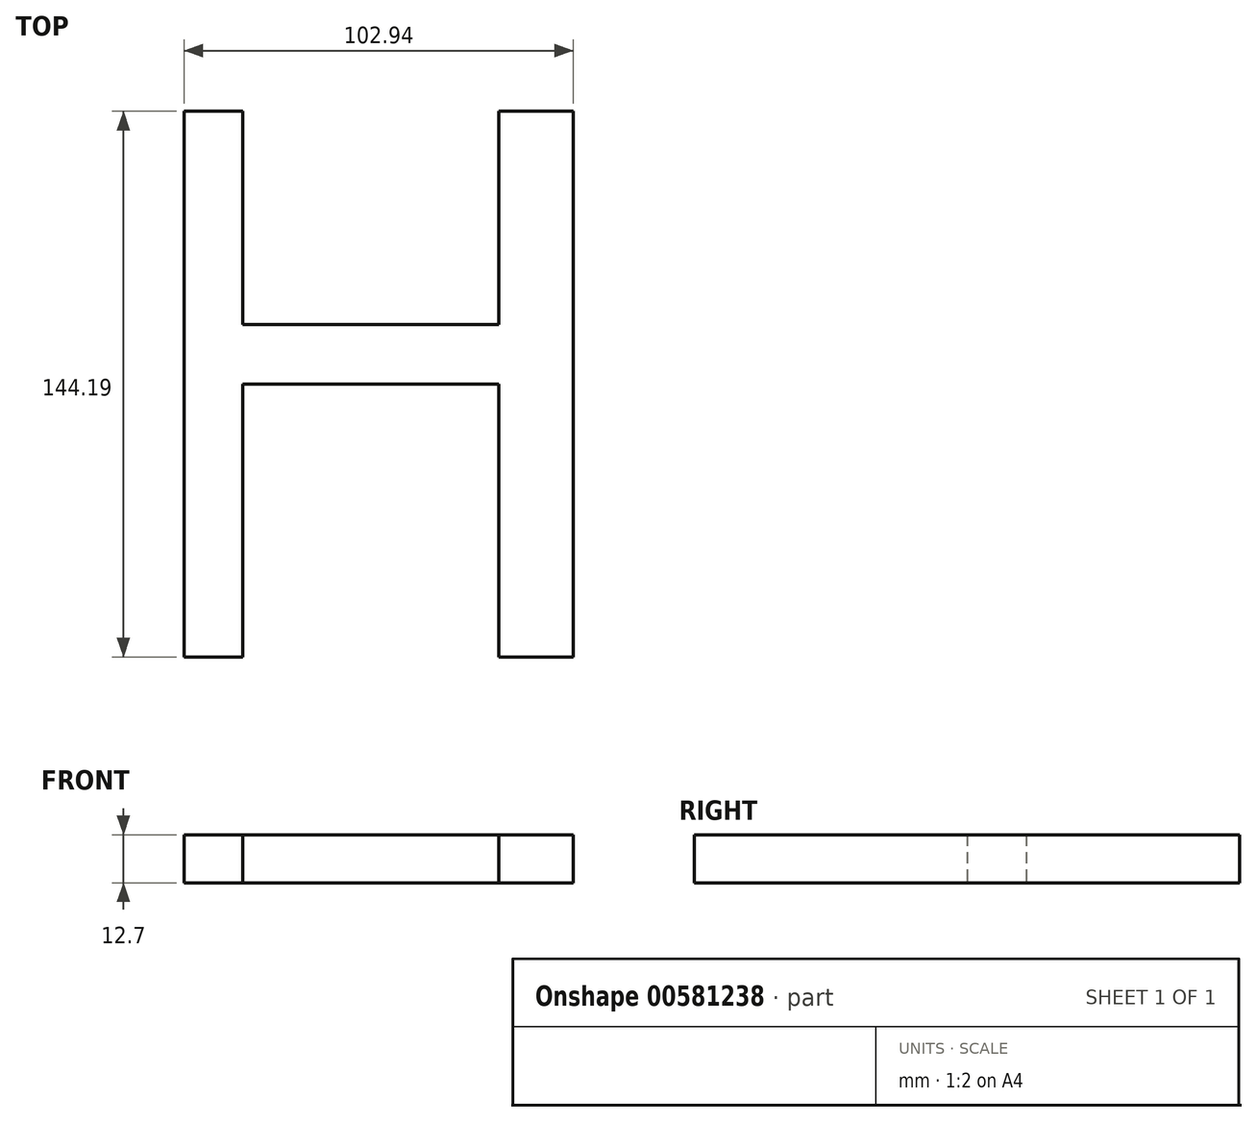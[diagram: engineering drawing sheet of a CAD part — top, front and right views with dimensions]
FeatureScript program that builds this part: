
annotation { "Feature Type Name" : "Feature", "Feature Type Description" : "" }
export const myFeature = defineFeature(function(context is Context, id is Id, definition is map)
    precondition{}
    {
        {
            var Q0;
            Q0=qCreatedBy(makeId("Top.planeOp"),FACE);
            var sketch = newSketch(context, id + "F0", { "sketchPlane" : qUnion([Q0])});
            skLineSegment(sketch, "E0.bottom", {"start": v(-384.94, 144.19) * mm, "end": v(-369.43, 144.19) * mm});
            skLineSegment(sketch, "E0.top", {"start": v(-384.94, 0) * mm, "end": v(-369.43, 0) * mm});
            skLineSegment(sketch, "E0.left", {"start": v(-384.94, 144.19) * mm, "end": v(-384.94, 0) * mm});
            skLineSegment(sketch, "E0.right", {"start": v(-369.43, 144.19) * mm, "end": v(-369.43, 0) * mm});
            skPoint(sketch, "E1.oppositeSnap0", {"position": v(-369.43, 72.1) * mm});
            skLineSegment(sketch, "E1.bottom", {"start": v(-369.43, 87.78) * mm, "end": v(-301.74, 87.78) * mm});
            skLineSegment(sketch, "E1.top", {"start": v(-369.43, 72.1) * mm, "end": v(-301.74, 72.1) * mm});
            skLineSegment(sketch, "E1.left", {"start": v(-369.43, 87.78) * mm, "end": v(-369.43, 72.1) * mm});
            skLineSegment(sketch, "E1.right", {"start": v(-301.74, 87.78) * mm, "end": v(-301.74, 72.1) * mm});
            skLineSegment(sketch, "E2.bottom", {"start": v(-301.74, 144.19) * mm, "end": v(-282, 144.19) * mm});
            skLineSegment(sketch, "E2.top", {"start": v(-301.74, 0) * mm, "end": v(-282, 0) * mm});
            skLineSegment(sketch, "E2.left", {"start": v(-301.74, 144.19) * mm, "end": v(-301.74, 0) * mm});
            skLineSegment(sketch, "E2.right", {"start": v(-282, 144.19) * mm, "end": v(-282, 0) * mm});
            skSolve(sketch);
        }
        {
            var Q0;
            Q0 = qSketchRegion(id + "F0", true);
            extrude(context, id + "F1", {"entities" : qUnion([Q0]), "depth" : 12.7 * mm, "offsetDistance" : 25.4 * mm});
        }
    });
